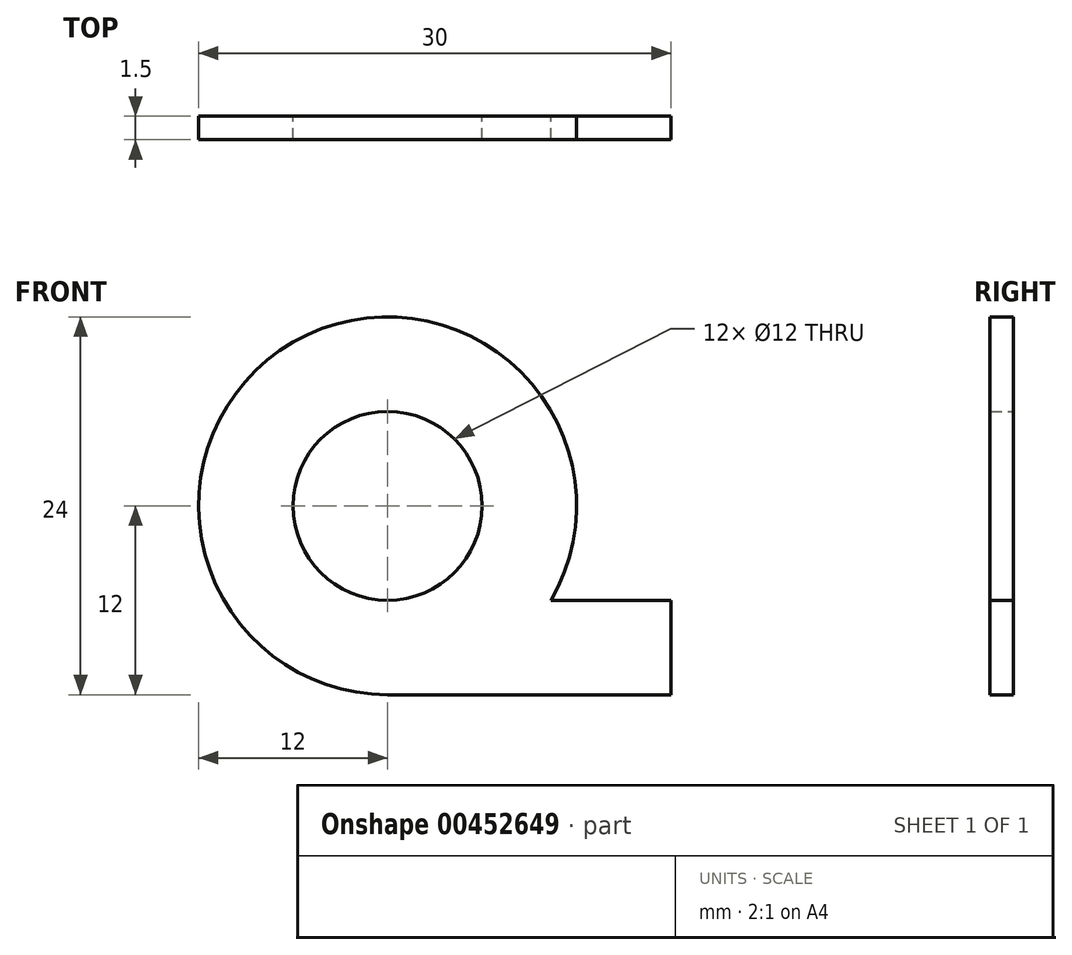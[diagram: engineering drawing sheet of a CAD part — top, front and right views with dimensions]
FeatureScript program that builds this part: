
annotation { "Feature Type Name" : "Feature", "Feature Type Description" : "" }
export const myFeature = defineFeature(function(context is Context, id is Id, definition is map)
    precondition{}
    {
        {
            var Q0;
            Q0=qCreatedBy(makeId("Front.planeOp"),FACE);
            var sketch = newSketch(context, id + "F0", { "sketchPlane" : qUnion([Q0])});
            skCircle(sketch, "E0", {"center": v(0, 0) * mm, "radius": 6 * mm});
            skCircle(sketch, "E1", {"center": v(0, 0) * mm, "radius": 12 * mm});
            skLineSegment(sketch, "E2.bottom", {"start": v(0, -12) * mm, "end": v(18, -12) * mm});
            skLineSegment(sketch, "E2.top", {"start": v(0, -6) * mm, "end": v(18, -6) * mm});
            skLineSegment(sketch, "E2.left", {"start": v(0, -12) * mm, "end": v(0, -6) * mm});
            skLineSegment(sketch, "E2.right", {"start": v(18, -12) * mm, "end": v(18, -6) * mm});
            skSolve(sketch);
        }
        {
            var Q0;
            {var subQ0=sQuery(id+"F0.wireOp",EDGE,"E0");Q0=makeQuery(id+"F0.imprint","IMPRINT",FACE,{"disambiguationData":[TD([[makeQuery(id+"F0.imprint","IMPRINT",EDGE,{"derivedFrom":subQ0}),-1.0]])]});}
            var Q1;
            {var subQ0=sQuery(id+"F0.wireOp",EDGE,"E2.bottom");Q1=makeQuery(id+"F0.imprint","IMPRINT",FACE,{"disambiguationData":[TD([[makeQuery(id+"F0.imprint","IMPRINT",EDGE,{"derivedFrom":subQ0}),1.0]])]});}
            var Q2;
            {var subQ0=sQuery(id+"F0.wireOp",EDGE,"E2.left");Q2=makeQuery(id+"F0.imprint","IMPRINT",FACE,{"disambiguationData":[TD([[makeQuery(id+"F0.imprint","IMPRINT",EDGE,{"derivedFrom":subQ0}),-1.0]])]});}
            extrude(context, id + "F1", {"entities" : qUnion([Q0, Q1, Q2]), "depth" : 1.5 * mm});
        }
    });
